# Revit family: NBS_HeatraeSadia_StrgWtrHtrsElctrc_Multipoint30and50Horizontal
name_source: partatom
category: Plumbing Fixtures
revit_build: Autodesk Revit 2014 (Build: 20130709_2115(x64)
units: mm (PartAtom-declared; Revit-internal decimal feet)

## types (2) — shared parameters
Accessories = Accessory pack U1 (95:970:352), Accessory pack U2 (95:970:351), Accessory pack U3 (95:970:354), Accessory pack U7 (95:970:360)
Arrangement = Multipoint – mains supply
AssetType = Fixed
CW Connection = Yes
CasingFinish = White stove enamel
Color = White
Connections = Heater: 15 mm copper tube tails; Tundish: Inlet - 1/2" BSP male, outlet - 3/4" BSP female; Service valve: 15 mm compression
Controls = For use with standard tap or mixer
Depth = 352 mm  [stored 1.15486 ft]
Description = Unvented point of use storage water heater
DurationUnit = year
Features = Element ‘on’ indicator, no anodes to inspect or replace, suitable for use with any standard tap or mixer, suitable replacement for cistern-type water heaters where improved water flow is required.
Fixing = Wall fixed
FlowRate = To suit draw off requirements
HW Connection = Yes
HeatTransferSurfaceArea = 0
Height = 370 mm  [stored 1.21391 ft]
IPCode = IPX4
IfcExportAs = IfcBoilerType
IfcExportType = WATER
IsWaterStorageHeater = Yes
ManufacturerName = Heatrae Sadia
ManufacturerURL = www.heatraesadia.com
Material = Outer casing: Plastic top and base mouldings with steel centre section; Water container: Heavy gauge copper; Heat unit: Replaceable rod-type element sheathed in corrosion resistant alloy
NBSCertification = http://www.nationalbimlibrary.com
NBSDescription = Storage water heaters, electric
NBSReference = 90-15-35/440
NominalLength = 370 mm  [stored 1.21391 ft]
NominalWidth = 352 mm  [stored 1.15486 ft]
OutletTemperatureRange = 5, 75
PartialLoadEfficiencyCurves = 0
PressureRating = 0
ProductInformation = www.heatraesadia.com/docs/POU_unvented_water_heating_brochure.pdf
Rating = 3.0 kW
SafetyFeatures = Manually re-settable thermal cut-out, temperature and pressure relief valve set to open at 7 bar or 90°C
StorageWaterHeaterMaterial = NBS_Concept
ThermalInsulation = CFC/HCFC free (ODP zero) flame-retardant expanded polyurethane
ThirdPartyCertification = Kiwa approved
Uniclass2 = 90-90-46/428
Uniclass2015Description = Electric storage water heaters
Uniclass2015Reference = Pr_60_60_96_28
Uniclass2015Version = Products v1.1
Vent Connection = No
Version = 1
WarrantyDurationParts = 5
WarrantyDurationUnit = year
WarrantyStartDate = 1900-12-31T23:59:59
WaterInletTemperatureRange = 0
zero-valued in all types: HeatOutput, NominalEfficiency, NominalEnergyConsumption, NominalPartLoadRatio

## per-type parameters (varying)
| type | BIMObjectName | BodyWidth | ModelNumber | ModelReference | Name | NominalHeight | Size | WaterStorageCapacity | Weight | Width |
| 30H-3kW | NBS_HeatraeSadia_StorageWaterHeatersElectric_Multipoint_30H-3kW | 616 mm  [stored 2.021 ft] | 95:050:154 | Multipoint 30H 3kW | StorageWaterHeatersElectric_Multipoint_30H-3kW_HeatraeSadia | 788 mm | 788 x 370 x 352 mm | 30 | 42.5 | 788 mm |
| 50H-3kW | NBS_HeatraeSadia_StorageWaterHeatersElectric_Multipoint_50H-3kW | 888 mm | 95:050:157 | Multipoint 50H 3kW | StorageWaterHeatersElectric_Multipoint_50H-3kW_HeatraeSadia | 1060 mm | 1060 x 370 x 352 mm | 50 | 69.3 | 1060 mm |

note: [stored X ft] marks values corroborated as IEEE doubles in the binary element streams (Revit-internal decimal feet)

## geometry (parser evidence)
native form markers: Sweep x3
no freeform markers — native parametric forms only
